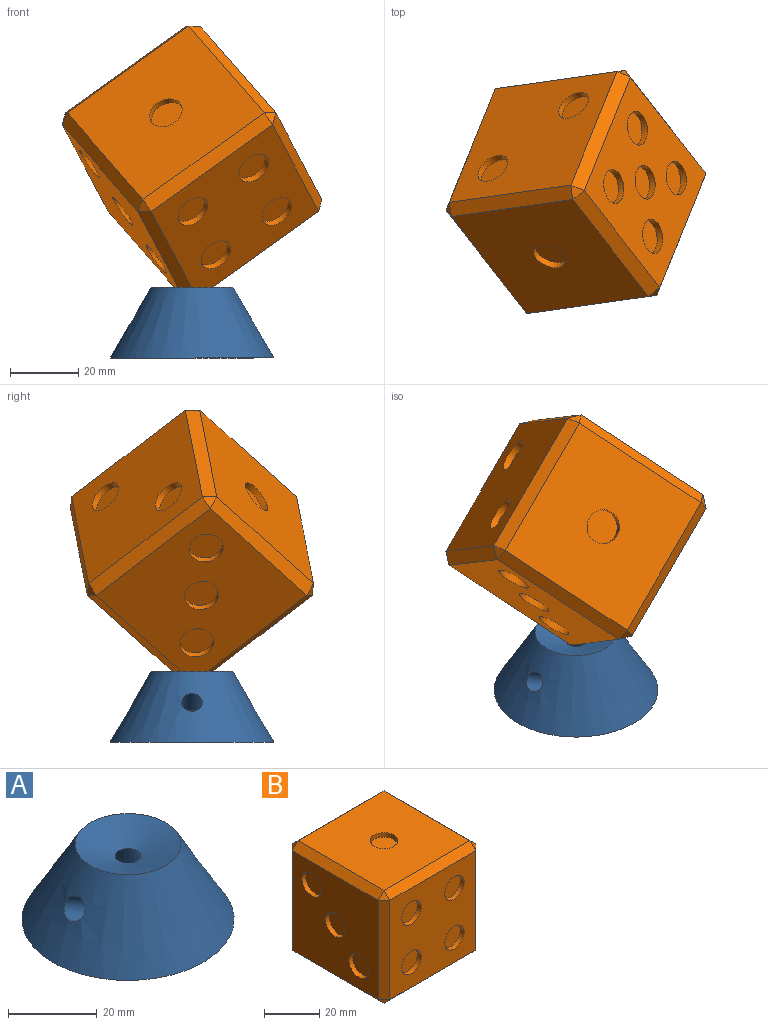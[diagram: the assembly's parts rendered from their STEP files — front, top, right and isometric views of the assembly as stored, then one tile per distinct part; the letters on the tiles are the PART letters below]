
ASSEMBLY  parts=2 mates=1
PART A: 5 faces, bbox 47.9x47.9x20.7 mm
  f0: cone r=2.91mm half-angle=27.4deg, axis (0,0,-1), area 893.8mm2, adj f2,f3,f4
  f1: cone r=11.98mm half-angle=30deg, axis (0,0,-1), area 2675.6mm2, adj f2,f3,f4
  f2: cone r=11.98mm half-angle=70.4deg, axis (0,0,1), area 450.2mm2, adj f0,f1
  f3: plane 47.91x47.91mm, normal (0,0,-1), area 1352mm2, adj f0,f1
  f4: cylinder r=3mm len=12.1mm, axis (0.87,0,-0.5), area 191.4mm2, adj f0,f1
PART B: 68 faces, bbox 50x50x50 mm
  f0: plane 44x44mm, normal (0,-1,0), area 1621.8mm2, adj f40,f42,f44,f46,f51,f52,f61,f62
  f1: plane 44x44mm, normal (1,0,0), area 1543.3mm2, adj f26,f28,f30,f32,f34,f48,f52,f53
  f2: plane 44x44mm, normal (0,0,-1), area 1464.8mm2, adj f8,f10,f12,f14,f16,f18,f53,f62
  f3: plane 44x44mm, normal (0,1,0), area 1778.9mm2, adj f36,f38,f54,f55,f63,f64
  f4: plane 44x44mm, normal (-1,0,0), area 1700.4mm2, adj f20,f22,f24,f56,f61,f64,f67
  f5: plane 44x44mm, normal (0,0,1), area 1857.5mm2, adj f6,f48,f51,f55,f56
  f6: cylinder r=5mm len=10mm, axis (0,0,1), area 62.8mm2, adj f5,f7
  f7: plane 10x10mm, normal (0,0,1), area 78.5mm2, adj f6
  f8: cylinder r=5mm len=10mm, axis (0,0,-1), area 62.8mm2, adj f2,f9
  f9: plane 10x10mm, normal (0,0,-1), area 78.5mm2, adj f8
  f10: cylinder r=5mm len=10mm, axis (0,0,-1), area 62.8mm2, adj f2,f11
  f11: plane 10x10mm, normal (0,0,-1), area 78.5mm2, adj f10
  f12: cylinder r=5mm len=10mm, axis (0,0,-1), area 62.8mm2, adj f2,f13
  f13: plane 10x10mm, normal (0,0,-1), area 78.5mm2, adj f12
  f14: cylinder r=5mm len=10mm, axis (0,0,-1), area 62.8mm2, adj f2,f15
  f15: plane 10x10mm, normal (0,0,-1), area 78.5mm2, adj f14
  f16: cylinder r=5mm len=10mm, axis (0,0,-1), area 62.8mm2, adj f2,f17
  f17: plane 10x10mm, normal (0,0,-1), area 78.5mm2, adj f16
  f18: cylinder r=5mm len=10mm, axis (0,0,-1), area 62.8mm2, adj f2,f19
  f19: plane 10x10mm, normal (0,0,-1), area 78.5mm2, adj f18
  f20: cylinder r=5mm len=10mm, axis (-1,0,0), area 62.8mm2, adj f4,f21
  f21: plane 10x10mm, normal (-1,0,0), area 78.5mm2, adj f20
  f22: cylinder r=5mm len=10mm, axis (-1,0,0), area 62.8mm2, adj f4,f23
  f23: plane 10x10mm, normal (-1,0,0), area 78.5mm2, adj f22
  f24: cylinder r=5mm len=10mm, axis (-1,0,0), area 62.8mm2, adj f4,f25
  f25: plane 10x10mm, normal (-1,0,0), area 78.5mm2, adj f24
  f26: cylinder r=5mm len=10mm, axis (1,0,0), area 62.8mm2, adj f1,f27
  f27: plane 10x10mm, normal (1,0,0), area 78.5mm2, adj f26
  f28: cylinder r=5mm len=10mm, axis (1,0,0), area 62.8mm2, adj f1,f29
  f29: plane 10x10mm, normal (1,0,0), area 78.5mm2, adj f28
  f30: cylinder r=5mm len=10mm, axis (1,0,0), area 62.8mm2, adj f1,f31
  f31: plane 10x10mm, normal (1,0,0), area 78.5mm2, adj f30
  f32: cylinder r=5mm len=10mm, axis (1,0,0), area 62.8mm2, adj f1,f33
  f33: plane 10x10mm, normal (1,0,0), area 78.5mm2, adj f32
  f34: cylinder r=5mm len=10mm, axis (1,0,0), area 62.8mm2, adj f1,f35
  f35: plane 10x10mm, normal (1,0,0), area 78.5mm2, adj f34
  f36: cylinder r=5mm len=10mm, axis (0,1,0), area 62.8mm2, adj f3,f37
  f37: plane 10x10mm, normal (0,1,0), area 78.5mm2, adj f36
  f38: cylinder r=5mm len=10mm, axis (0,1,0), area 62.8mm2, adj f3,f39
  f39: plane 10x10mm, normal (0,1,0), area 78.5mm2, adj f38
  f40: cylinder r=5mm len=10mm, axis (0,-1,0), area 62.8mm2, adj f0,f41
  f41: plane 10x10mm, normal (0,-1,0), area 78.5mm2, adj f40
  f42: cylinder r=5mm len=10mm, axis (0,-1,0), area 62.8mm2, adj f0,f43
  f43: plane 10x10mm, normal (0,-1,0), area 78.5mm2, adj f42
  f44: cylinder r=5mm len=10mm, axis (0,-1,0), area 62.8mm2, adj f0,f45
  f45: plane 10x10mm, normal (0,-1,0), area 78.5mm2, adj f44
  f46: cylinder r=5mm len=10mm, axis (0,-1,0), area 62.8mm2, adj f0,f47
  f47: plane 10x10mm, normal (0,-1,0), area 78.5mm2, adj f46
  f48: plane 44x3mm, normal (0.71,0,0.71), area 186.7mm2, adj f1,f5,f49,f50
  f49: plane 3x3mm, normal (0.58,-0.58,0.58), area 7.8mm2, adj f48,f51,f52
  f50: plane 3x3mm, normal (0.58,0.58,0.58), area 7.8mm2, adj f48,f54,f55
  f51: plane 44x3mm, normal (0,-0.71,0.71), area 186.7mm2, adj f0,f5,f49,f57
  f52: plane 44x3mm, normal (0.71,-0.71,0), area 186.7mm2, adj f0,f1,f49,f58
  f53: plane 44x3mm, normal (0.71,0,-0.71), area 186.7mm2, adj f1,f2,f58,f59
  f54: plane 44x3mm, normal (0.71,0.71,0), area 186.7mm2, adj f1,f3,f50,f59
  f55: plane 44x3mm, normal (0,0.71,0.71), area 186.7mm2, adj f3,f5,f50,f60
  f56: plane 44x3mm, normal (-0.71,0,0.71), area 186.7mm2, adj f4,f5,f57,f60
  f57: plane 3x3mm, normal (-0.58,-0.58,0.58), area 7.8mm2, adj f51,f56,f61
  f58: plane 3x3mm, normal (0.58,-0.58,-0.58), area 7.8mm2, adj f52,f53,f62
  f59: plane 3x3mm, normal (0.58,0.58,-0.58), area 7.8mm2, adj f53,f54,f63
  f60: plane 3x3mm, normal (-0.58,0.58,0.58), area 7.8mm2, adj f55,f56,f64
  f61: plane 44x3mm, normal (-0.71,-0.71,0), area 186.7mm2, adj f0,f4,f57,f65
  f62: plane 44x3mm, normal (0,-0.71,-0.71), area 186.7mm2, adj f0,f2,f58,f65
  f63: plane 44x3mm, normal (0,0.71,-0.71), area 186.7mm2, adj f2,f3,f59,f66
  f64: plane 44x3mm, normal (-0.71,0.71,0), area 186.7mm2, adj f3,f4,f60,f66
  f65: plane 3x3mm, normal (-0.58,-0.58,-0.58), area 7.8mm2, adj f61,f62,f67
  f66: plane 3x3mm, normal (-0.58,0.58,-0.58), area 7.8mm2, adj f63,f64,f67
  f67: plane 44x3mm, normal (-0.71,0,-0.71), area 186.7mm2, adj f2,f4,f65,f66
PLACE A at identity fixed
PLACE B rot(axis=(0.78,-0.52,0.36),59deg) t=(0,0,57.35)mm
MATE cylindrical B.f65 <-> A.f0  axis (0,0,-1) through (0,0,17.51)mm
